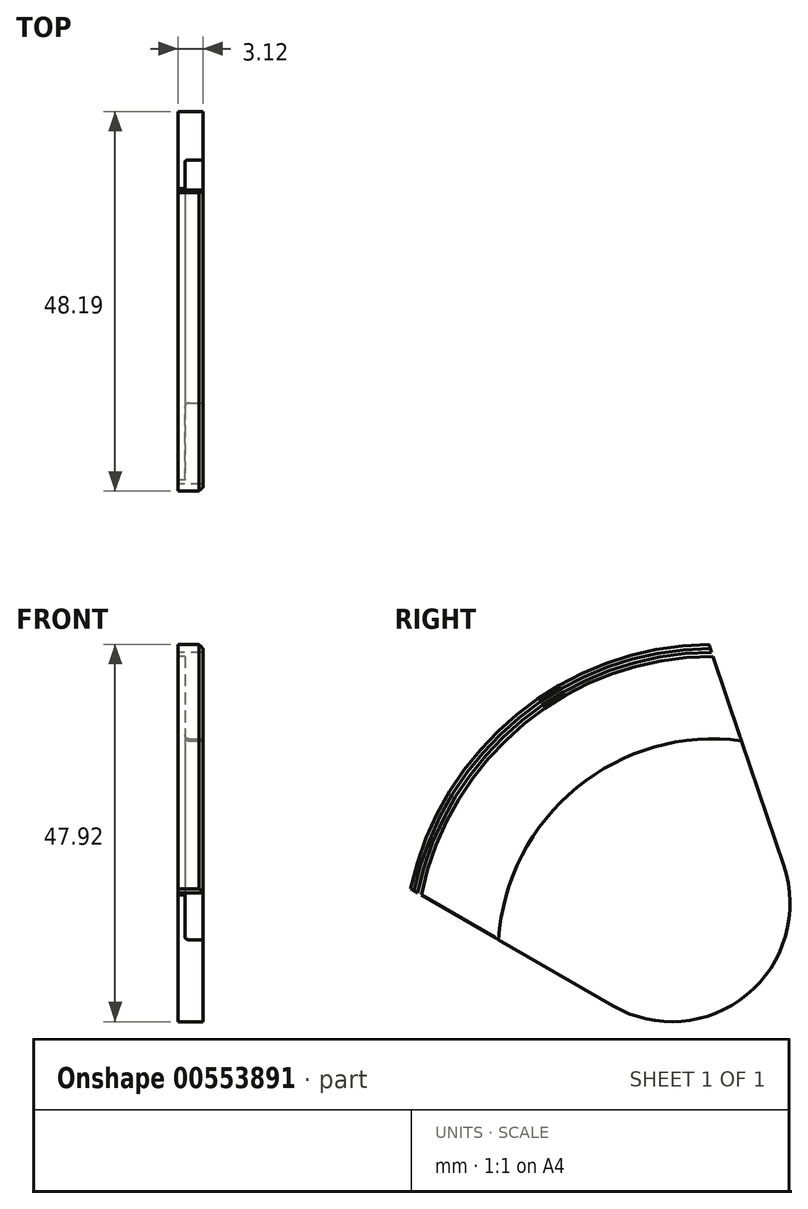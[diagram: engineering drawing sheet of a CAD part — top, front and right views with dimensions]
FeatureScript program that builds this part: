
annotation { "Feature Type Name" : "Feature", "Feature Type Description" : "" }
export const myFeature = defineFeature(function(context is Context, id is Id, definition is map)
    precondition{}
    {
        {
            var Q0;
            Q0=qCreatedBy(makeId("Right.planeOp"),FACE);
            var sketch = newSketch(context, id + "F0", { "sketchPlane" : qUnion([Q0])});
            skLineSegment(sketch, "E0", {"start": v(-70.5, 81.28) * mm, "end": v(-46.56, 52.03) * mm});
            skLineSegment(sketch, "E1", {"start": v(-46.56, 52.03) * mm, "end": v(-24.84, 25.5) * mm});
            skLineSegment(sketch, "E2", {"start": v(-46.56, 89.83) * mm, "end": v(-37.58, 63.21) * mm});
            skLineSegment(sketch, "E3", {"start": v(-83.62, 59.5) * mm, "end": v(-59.3, 45.43) * mm});
            skPoint(sketch, "E4.visualSharp", {"position": v(-24.84, 25.5) * mm});
            skArc(sketch, "E4.filletArc", {"start": v(-59.3, 45.43) * mm, "mid": v(-42.29, 46.8) * mm, "end": v(-37.58, 63.21) * mm});
            skArc(sketch, "E5", {"start": v(-46.56, 89.83) * mm, "mid": v(-70.5, 81.28) * mm, "end": v(-83.62, 59.5) * mm});
            skSolve(sketch);
        }
        {
            var Q0;
            Q0 = qSketchRegion(id + "F0", true);
            extrude(context, id + "F1", {"entities" : qUnion([Q0]), "depth" : 2.37 * mm, "offsetDistance" : 25 * mm});
        }
        {
            var Q0;
            Q0=makeQuery(id+"F1.opExtrude","CAP_FACE",FACE,{"disambiguationData":[OSD([sQuery(id+"F0.wireOp",EDGE,"E2"),sQuery(id+"F0.wireOp",EDGE,"E3"),sQuery(id+"F0.wireOp",EDGE,"E4.filletArc"),sQuery(id+"F0.wireOp",EDGE,"E5")])],"isStart":true});
            var sketch = newSketch(context, id + "F2", { "sketchPlane" : qUnion([Q0])});
            skArc(sketch, "E6.0", {"start": v(47.07, 91.33) * mm, "mid": v(71.45, 82.44) * mm, "end": v(84.98, 60.3) * mm});
            skArc(sketch, "E7.0", {"start": v(46.73, 90.33) * mm, "mid": v(70.82, 81.67) * mm, "end": v(84.07, 59.77) * mm});
            skLineSegment(sketch, "E8", {"start": v(37.58, 63.21) * mm, "end": v(47.07, 91.33) * mm});
            skLineSegment(sketch, "E9", {"start": v(59.3, 45.43) * mm, "end": v(84.98, 60.3) * mm});
            skArc(sketch, "E10.0", {"start": v(42.93, 79.09) * mm, "mid": v(63.85, 73.16) * mm, "end": v(73.8, 53.82) * mm});
            skArc(sketch, "E11.0", {"start": v(42.58, 78.03) * mm, "mid": v(63.22, 72.38) * mm, "end": v(72.83, 53.26) * mm});
            skSolve(sketch);
        }
        {
            var Q0;
            {var subQ0=sQuery(id+"F2.wireOp",EDGE,"E7.0");Q0=makeQuery(id+"F2.imprint","IMPRINT",FACE,{"disambiguationData":[TD([[makeQuery(id+"F2.imprint","IMPRINT",EDGE,{"derivedFrom":subQ0}),-1.0]])]});}
            var Q1;
            {var subQ0=sQuery(id+"F2.wireOp",EDGE,"E6.0");Q1=makeQuery(id+"F2.imprint","IMPRINT",FACE,{"disambiguationData":[TD([[makeQuery(id+"F2.imprint","IMPRINT",EDGE,{"derivedFrom":subQ0}),-1.0]])]});}
            extrude(context, id + "F3", {"entities" : qUnion([Q0, Q1]), "operationType" : NewBodyOperationType.ADD, "oppositeDirection" : true, "depth" : 2.37 * mm, "offsetDistance" : 25 * mm});
        }
        {
            var Q0;
            {var subQ0=sQuery(id+"F0.wireOp",EDGE,"E5");Q0=makeQuery(id+"F3.boolean.opBoolean","MERGE",FACE,{"derivedFrom":[makeQuery(id+"F1.opExtrude","CAP_FACE",FACE,{"disambiguationData":[OSD([sQuery(id+"F0.wireOp",EDGE,"E2"),sQuery(id+"F0.wireOp",EDGE,"E3"),sQuery(id+"F0.wireOp",EDGE,"E4.filletArc"),subQ0])],"isStart":false}),makeQuery(id+"F3.opExtrude","CAP_FACE",FACE,{"disambiguationData":[OSD([subQ0,sQuery(id+"F2.wireOp",EDGE,"E6.0"),sQuery(id+"F2.wireOp",EDGE,"E8"),sQuery(id+"F2.wireOp",EDGE,"E9")])],"isStart":false})]});}
            var sketch = newSketch(context, id + "F4", { "sketchPlane" : qUnion([Q0])});
            skArc(sketch, "E12.0", {"start": v(-42.93, 79.09) * mm, "mid": v(-63.85, 73.16) * mm, "end": v(-73.8, 53.82) * mm});
            skArc(sketch, "E13.converted", {"start": v(-46.73, 90.33) * mm, "mid": v(-70.82, 81.67) * mm, "end": v(-84.07, 59.77) * mm});
            skLineSegment(sketch, "E14", {"start": v(-73.8, 53.82) * mm, "end": v(-84.07, 59.77) * mm});
            skSolve(sketch);
        }
        {
            var Q0;
            {var subQ0=sQuery(id+"F4.wireOp",EDGE,"E12.0");Q0=makeQuery(id+"F4.imprint","IMPRINT",FACE,{"disambiguationData":[TD([[makeQuery(id+"F4.imprint","IMPRINT",EDGE,{"derivedFrom":subQ0}),-1.0]])]});}
            extrude(context, id + "F5", {"entities" : qUnion([Q0]), "operationType" : NewBodyOperationType.REMOVE, "oppositeDirection" : true, "depth" : 2.25 * mm, "offsetDistance" : 25 * mm});
        }
        {
            var Q0;
            {var subQ0=sQuery(id+"F0.wireOp",EDGE,"E5");Q0=makeQuery(id+"F3.boolean.opBoolean","MERGE",FACE,{"derivedFrom":[makeQuery(id+"F1.opExtrude","CAP_FACE",FACE,{"disambiguationData":[OSD([sQuery(id+"F0.wireOp",EDGE,"E2"),sQuery(id+"F0.wireOp",EDGE,"E3"),sQuery(id+"F0.wireOp",EDGE,"E4.filletArc"),subQ0])],"isStart":true}),makeQuery(id+"F3.opExtrude","CAP_FACE",FACE,{"disambiguationData":[OSD([subQ0,sQuery(id+"F2.wireOp",EDGE,"E6.0"),sQuery(id+"F2.wireOp",EDGE,"E8"),sQuery(id+"F2.wireOp",EDGE,"E9")])],"isStart":true})]});}
            extrude(context, id + "F6", {"entities" : qUnion([Q0]), "operationType" : NewBodyOperationType.ADD, "depth" : .75 * mm, "offsetDistance" : 25 * mm});
        }
        {
            var Q0;
            Q0=makeQuery(id+"F3.opExtrude","CAP_EDGE",EDGE,{"disambiguationData":[OSD([sQuery(id+"F2.wireOp",EDGE,"E6.0")])],"isStart":false});
            var Q1;
            Q1=makeQuery(id+"F5.boolean.opBoolean","COPY",EDGE,{"derivedFrom":makeQuery(id+"F5.opExtrude","CAP_EDGE",EDGE,{"disambiguationData":[OSD([sQuery(id+"F4.wireOp",EDGE,"E12.0")])],"isStart":true})});
            chamfer(context, id + "F7", {"entities" : qUnion([Q0, Q1]), "width" : .5 * mm, "tangentPropagation" : true});
        }
        {
            var Q0;
            Q0=makeQuery(id+"F5.boolean.opBoolean","COPY",EDGE,{"derivedFrom":makeQuery(id+"F5.opExtrude","CAP_EDGE",EDGE,{"disambiguationData":[OSD([sQuery(id+"F4.wireOp",EDGE,"E13.converted")])],"isStart":false})});
            var Q1;
            Q1=makeQuery(id+"F5.boolean.opBoolean","COPY",EDGE,{"derivedFrom":makeQuery(id+"F5.opExtrude","CAP_EDGE",EDGE,{"disambiguationData":[OSD([sQuery(id+"F4.wireOp",EDGE,"E12.0")])],"isStart":false})});
            fillet(context, id + "F8", {"entities" : qUnion([Q0, Q1]), "radius" : .5 * mm, "tangentPropagation" : true, "allowEdgeOverflow" : false});
        }
    });
